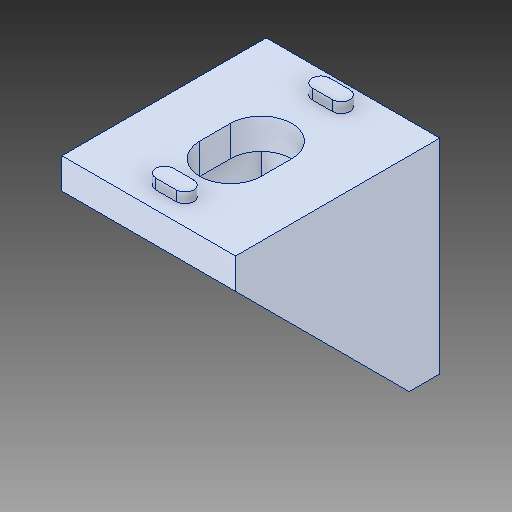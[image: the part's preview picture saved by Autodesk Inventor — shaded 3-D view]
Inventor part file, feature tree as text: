
AUTODESK INVENTOR PART (.ipt)
format: ipt  version: 2018 (Build 220112000, 112)  size: 144,896 bytes
history: mixed  units: mm
features: mirror x1, imported_body x1
ambient origin geometry x8: Origin, YZ Plane, XZ Plane, XY Plane, X Axis, Y Axis, Z Axis, Center Point
bodies: Solid1 (imported_parasolid)
feature tree (2):
  mirror  "Mirror1"
  imported_body  NMx_Import_Brep_tag  [imported B-rep: ~40 faces, bbox_mm=[17.0, 21.0, 21.0]]
